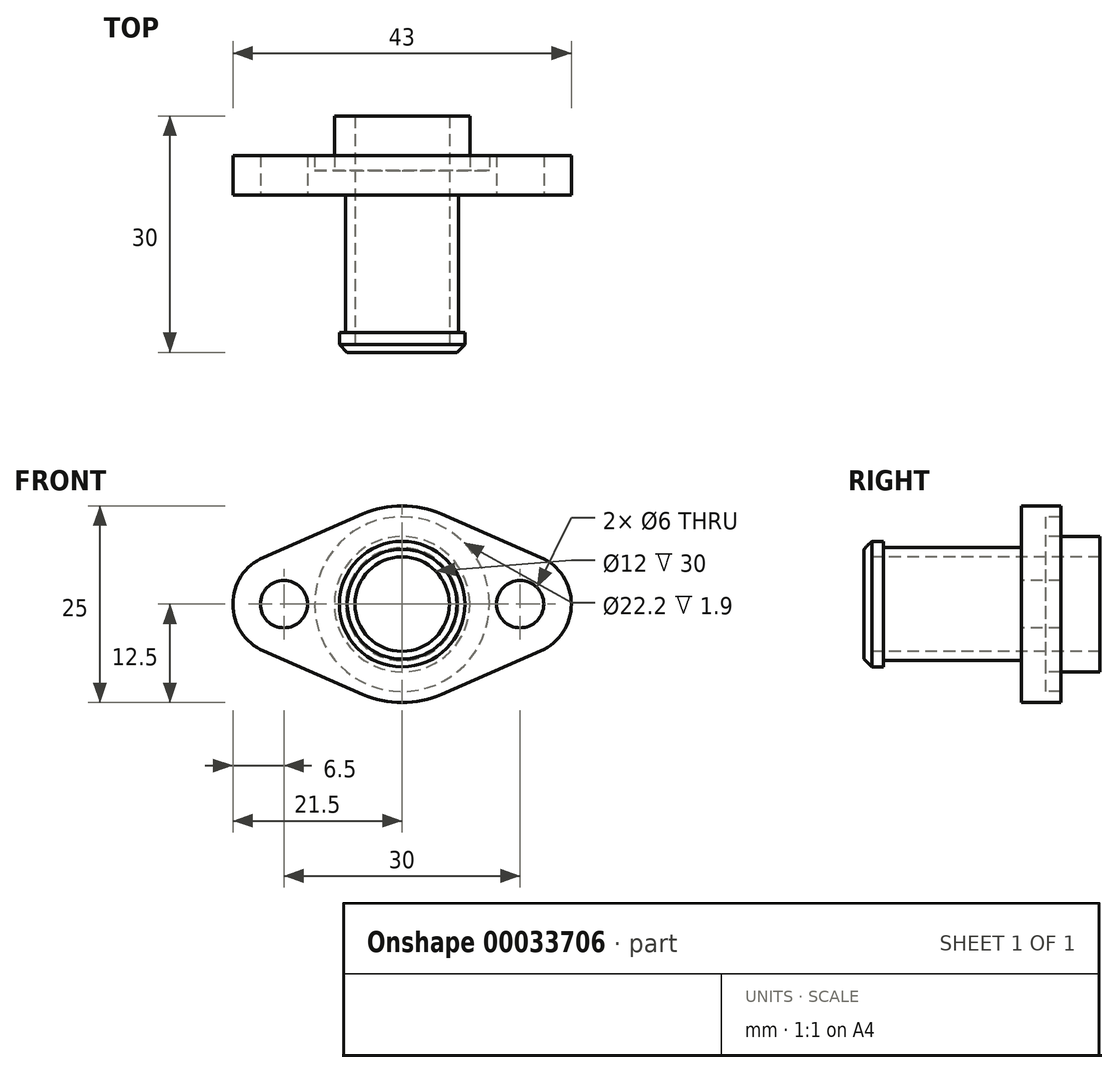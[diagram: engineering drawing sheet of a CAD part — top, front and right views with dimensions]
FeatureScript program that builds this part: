
annotation { "Feature Type Name" : "Feature", "Feature Type Description" : "" }
export const myFeature = defineFeature(function(context is Context, id is Id, definition is map)
    precondition{}
    {
        {
            var Q0;
            Q0=qCreatedBy(makeId("Right.planeOp"),FACE);
            var sketch = newSketch(context, id + "F0", { "sketchPlane" : qUnion([Q0])});
            skLineSegment(sketch, "E0", {"start": v(-20, 0) * mm, "end": v(11.7, 0) * mm, "construction": true});
            skLineSegment(sketch, "E1", {"start": v(-20, 6) * mm, "end": v(10, 6) * mm});
            skLineSegment(sketch, "E2", {"start": v(10, 6) * mm, "end": v(10, 8.6) * mm});
            skLineSegment(sketch, "E3", {"start": v(5, 11.1) * mm, "end": v(5, 21.5) * mm});
            skLineSegment(sketch, "E4", {"start": v(5, 21.5) * mm, "end": v(0, 21.5) * mm});
            skLineSegment(sketch, "E5", {"start": v(0, 21.5) * mm, "end": v(0, 7.17) * mm});
            skLineSegment(sketch, "E6", {"start": v(0, 7.17) * mm, "end": v(-17.5, 7.17) * mm});
            skLineSegment(sketch, "E7", {"start": v(-17.5, 7.17) * mm, "end": v(-17.5, 7.97) * mm});
            skLineSegment(sketch, "E8", {"start": v(-17.5, 7.97) * mm, "end": v(-20, 7.97) * mm});
            skLineSegment(sketch, "E9", {"start": v(-20, 7.97) * mm, "end": v(-20, 6) * mm});
            skPoint(sketch, "E10.end.orphan", {"position": v(7.97, 8.6) * mm});
            skPoint(sketch, "E11.orphan", {"position": v(6.44, 8.6) * mm});
            skLineSegment(sketch, "E12", {"start": v(10, 8.6) * mm, "end": v(3.1, 8.6) * mm});
            skLineSegment(sketch, "E13", {"start": v(3.1, 8.6) * mm, "end": v(3.1, 11.1) * mm});
            skLineSegment(sketch, "E14", {"start": v(3.1, 11.1) * mm, "end": v(5, 11.1) * mm});
            skPoint(sketch, "E15.orphan", {"position": v(5, 7.17) * mm});
            skSolve(sketch);
        }
        {
            var Q0;
            Q0=qSketchRegion(id+"F0",true);
            var Q1;
            Q1=sQuery(id+"F0.wireOp",EDGE,"E0");
            revolve(context, id + "F1", {"entities" : qUnion([Q0]), "axis" : qUnion([Q1]), "revolveType" : RevolveType.FULL});
        }
        {
            var Q0;
            Q0=makeQuery(id+"F1.opRevolve","SWEPT_EDGE",EDGE,{"disambiguationData":[OSD([sQuery(id+"F0.wireOp",EDGE,"E8"),sQuery(id+"F0.wireOp",EDGE,"E9")])]});
            chamfer(context, id + "F2", {"entities" : qUnion([Q0]), "width" : 1 * mm, "tangentPropagation" : true});
        }
        {
            var Q0;
            Q0=makeQuery(id+"F1.opRevolve","SWEPT_FACE",FACE,{"disambiguationData":[OSD([sQuery(id+"F0.wireOp",EDGE,"E5")])]});
            var sketch = newSketch(context, id + "F3", { "sketchPlane" : qUnion([Q0])});
            skCircle(sketch, "E16", {"center": v(-15, 0) * mm, "radius": 3 * mm});
            skCircle(sketch, "E17", {"center": v(15, 0) * mm, "radius": 3 * mm});
            skCircle(sketch, "E18", {"center": v(0, 0) * mm, "radius": 15 * mm, "construction": true});
            skArc(sketch, "E19", {"start": v(-17.6, 5.96) * mm, "mid": v(-21.5, 0) * mm, "end": v(-17.6, -5.96) * mm});
            skArc(sketch, "E20", {"start": v(17.6, -5.96) * mm, "mid": v(21.5, 0) * mm, "end": v(17.6, 5.96) * mm});
            skLineSegment(sketch, "E21", {"start": v(-17.6, 5.96) * mm, "end": v(-5, 11.46) * mm});
            skLineSegment(sketch, "E22", {"start": v(-17.6, -5.96) * mm, "end": v(-5, -11.46) * mm});
            skLineSegment(sketch, "E23", {"start": v(5, 11.46) * mm, "end": v(17.6, 5.96) * mm});
            skLineSegment(sketch, "E24", {"start": v(5, -11.46) * mm, "end": v(17.6, -5.96) * mm});
            skArc(sketch, "E25.trimOffspring", {"start": v(-5, -11.46) * mm, "mid": v(0, -12.5) * mm, "end": v(5, -11.46) * mm});
            skArc(sketch, "E26.trimOffspring", {"start": v(5, 11.46) * mm, "mid": v(0, 12.5) * mm, "end": v(-5, 11.46) * mm});
            skCircle(sketch, "E27", {"center": v(0, 0) * mm, "radius": 30 * mm});
            skSolve(sketch);
        }
        {
            var Q0;
            Q0=qSketchRegion(id+"F3",true);
            extrude(context, id + "F4", {"entities" : qUnion([Q0]), "operationType" : NewBodyOperationType.REMOVE, "oppositeDirection" : true, "depth" : 25 * mm});
        }
        {
            var Q0;
            Q0=makeQuery(id+"F3.imprint","IMPRINT",FACE,{"disambiguationData":[TD([[makeQuery(id+"F3.imprint","IMPRINT",EDGE,{"derivedFrom":sQuery(id+"F3.wireOp",EDGE,"E17")}),1.0]])]});
            var Q1;
            Q1=makeQuery(id+"F3.imprint","IMPRINT",FACE,{"disambiguationData":[TD([[makeQuery(id+"F3.imprint","IMPRINT",EDGE,{"derivedFrom":sQuery(id+"F3.wireOp",EDGE,"E16")}),1.0]])]});
            extrude(context, id + "F5", {"entities" : qUnion([Q0, Q1]), "operationType" : NewBodyOperationType.REMOVE, "oppositeDirection" : true, "depth" : 25 * mm});
        }
    });
